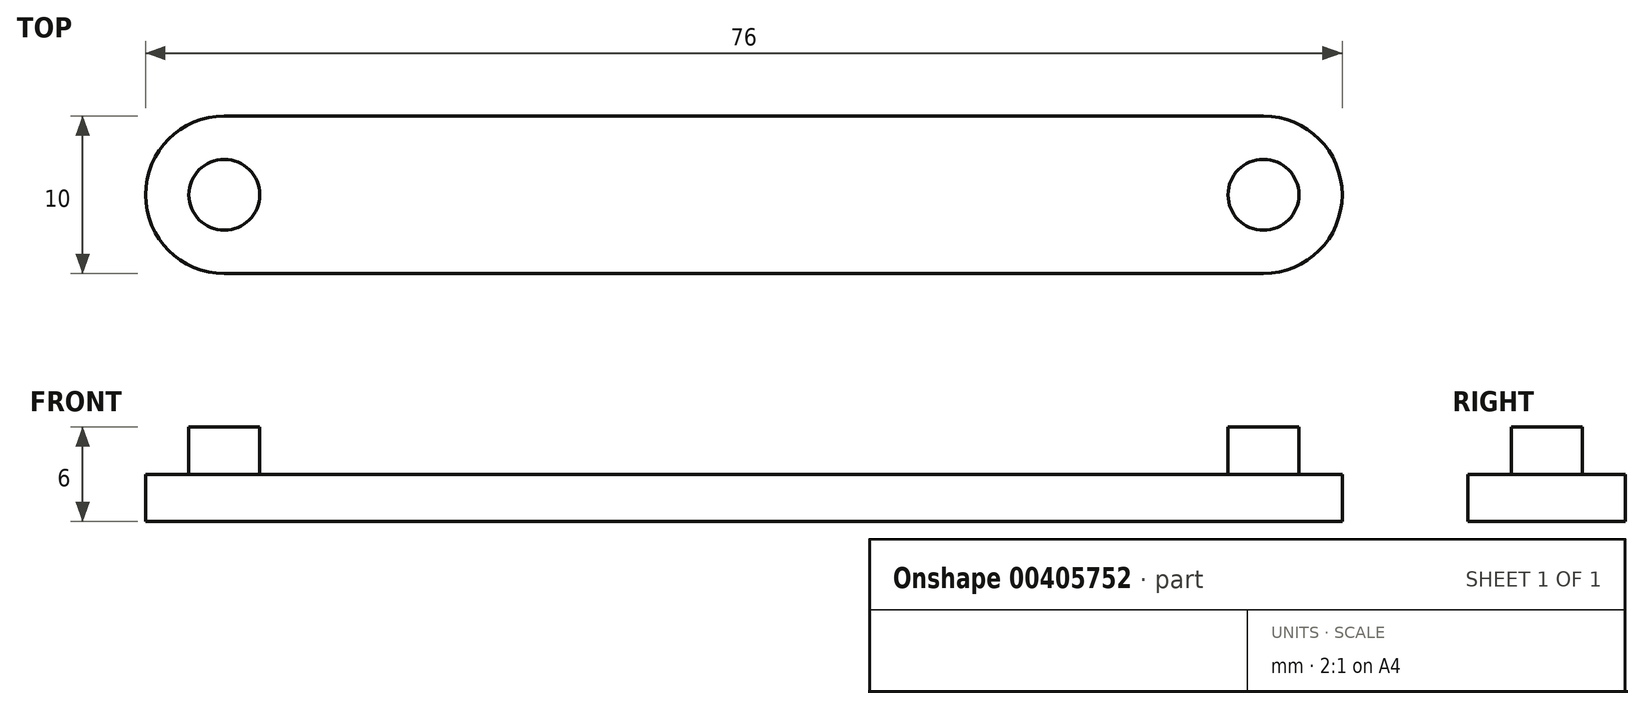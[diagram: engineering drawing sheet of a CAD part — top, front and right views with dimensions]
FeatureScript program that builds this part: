
annotation { "Feature Type Name" : "Feature", "Feature Type Description" : "" }
export const myFeature = defineFeature(function(context is Context, id is Id, definition is map)
    precondition{}
    {
        {
            var Q0;
            Q0=qCreatedBy(makeId("Top.planeOp"),FACE);
            var sketch = newSketch(context, id + "F0", { "sketchPlane" : qUnion([Q0])});
            skLineSegment(sketch, "E0.bottom", {"start": v(-33, 5) * mm, "end": v(33, 5) * mm});
            skLineSegment(sketch, "E0.top", {"start": v(-33, -5) * mm, "end": v(33, -5) * mm});
            skLineSegment(sketch, "E0.left", {"start": v(-33, 5) * mm, "end": v(-33, -5) * mm});
            skLineSegment(sketch, "E0.right", {"start": v(33, 5) * mm, "end": v(33, -5) * mm});
            skCircle(sketch, "E1", {"center": v(-33, 0) * mm, "radius": 5 * mm});
            skCircle(sketch, "E2", {"center": v(33, 0) * mm, "radius": 5 * mm});
            skLineSegment(sketch, "E3", {"start": v(-33, 5) * mm, "end": v(33, -5) * mm, "construction": true});
            skPoint(sketch, "E4", {"position": v(0, 0) * mm});
            skSolve(sketch);
        }
        {
            var Q0;
            {var subQ0=sQuery(id+"F0.wireOp",EDGE,"E0.left");Q0=makeQuery(id+"F0.imprint","IMPRINT",FACE,{"disambiguationData":[TD([[makeQuery(id+"F0.imprint","IMPRINT",EDGE,{"derivedFrom":subQ0}),-1.0]])]});}
            var Q1;
            {var subQ0=sQuery(id+"F0.wireOp",EDGE,"E0.left");Q1=makeQuery(id+"F0.imprint","IMPRINT",FACE,{"disambiguationData":[TD([[makeQuery(id+"F0.imprint","IMPRINT",EDGE,{"derivedFrom":subQ0}),1.0]])]});}
            var Q2;
            {var subQ0=sQuery(id+"F0.wireOp",EDGE,"E0.bottom");Q2=makeQuery(id+"F0.imprint","IMPRINT",FACE,{"disambiguationData":[TD([[makeQuery(id+"F0.imprint","IMPRINT",EDGE,{"derivedFrom":subQ0}),-1.0]])]});}
            var Q3;
            {var subQ0=sQuery(id+"F0.wireOp",EDGE,"E0.right");Q3=makeQuery(id+"F0.imprint","IMPRINT",FACE,{"disambiguationData":[TD([[makeQuery(id+"F0.imprint","IMPRINT",EDGE,{"derivedFrom":subQ0}),-1.0]])]});}
            var Q4;
            {var subQ0=sQuery(id+"F0.wireOp",EDGE,"E0.right");Q4=makeQuery(id+"F0.imprint","IMPRINT",FACE,{"disambiguationData":[TD([[makeQuery(id+"F0.imprint","IMPRINT",EDGE,{"derivedFrom":subQ0}),1.0]])]});}
            extrude(context, id + "F1", {"entities" : qUnion([Q0, Q1, Q2, Q3, Q4]), "depth" : 3 * mm});
        }
        {
            var Q0;
            Q0=makeQuery(id+"F1.opExtrude","CAP_FACE",FACE,{"disambiguationData":[OSD([sQuery(id+"F0.wireOp",EDGE,"E0.bottom"),sQuery(id+"F0.wireOp",EDGE,"E0.top"),sQuery(id+"F0.wireOp",EDGE,"E1"),sQuery(id+"F0.wireOp",EDGE,"E2")])],"isStart":false});
            var sketch = newSketch(context, id + "F2", { "sketchPlane" : qUnion([Q0])});
            skCircle(sketch, "E5", {"center": v(-33, 0) * mm, "radius": 2.25 * mm});
            skCircle(sketch, "E6", {"center": v(33, 0) * mm, "radius": 2.25 * mm});
            skSolve(sketch);
        }
        {
            var Q0;
            Q0=makeQuery(id+"F2.imprint","IMPRINT",FACE,{"disambiguationData":[TD([[makeQuery(id+"F2.imprint","IMPRINT",EDGE,{"derivedFrom":sQuery(id+"F2.wireOp",EDGE,"E5")}),1.0]])]});
            var Q1;
            Q1=makeQuery(id+"F2.imprint","IMPRINT",FACE,{"disambiguationData":[TD([[makeQuery(id+"F2.imprint","IMPRINT",EDGE,{"derivedFrom":sQuery(id+"F2.wireOp",EDGE,"E6")}),1.0]])]});
            extrude(context, id + "F3", {"entities" : qUnion([Q0, Q1]), "operationType" : NewBodyOperationType.ADD, "depth" : 3 * mm});
        }
    });
